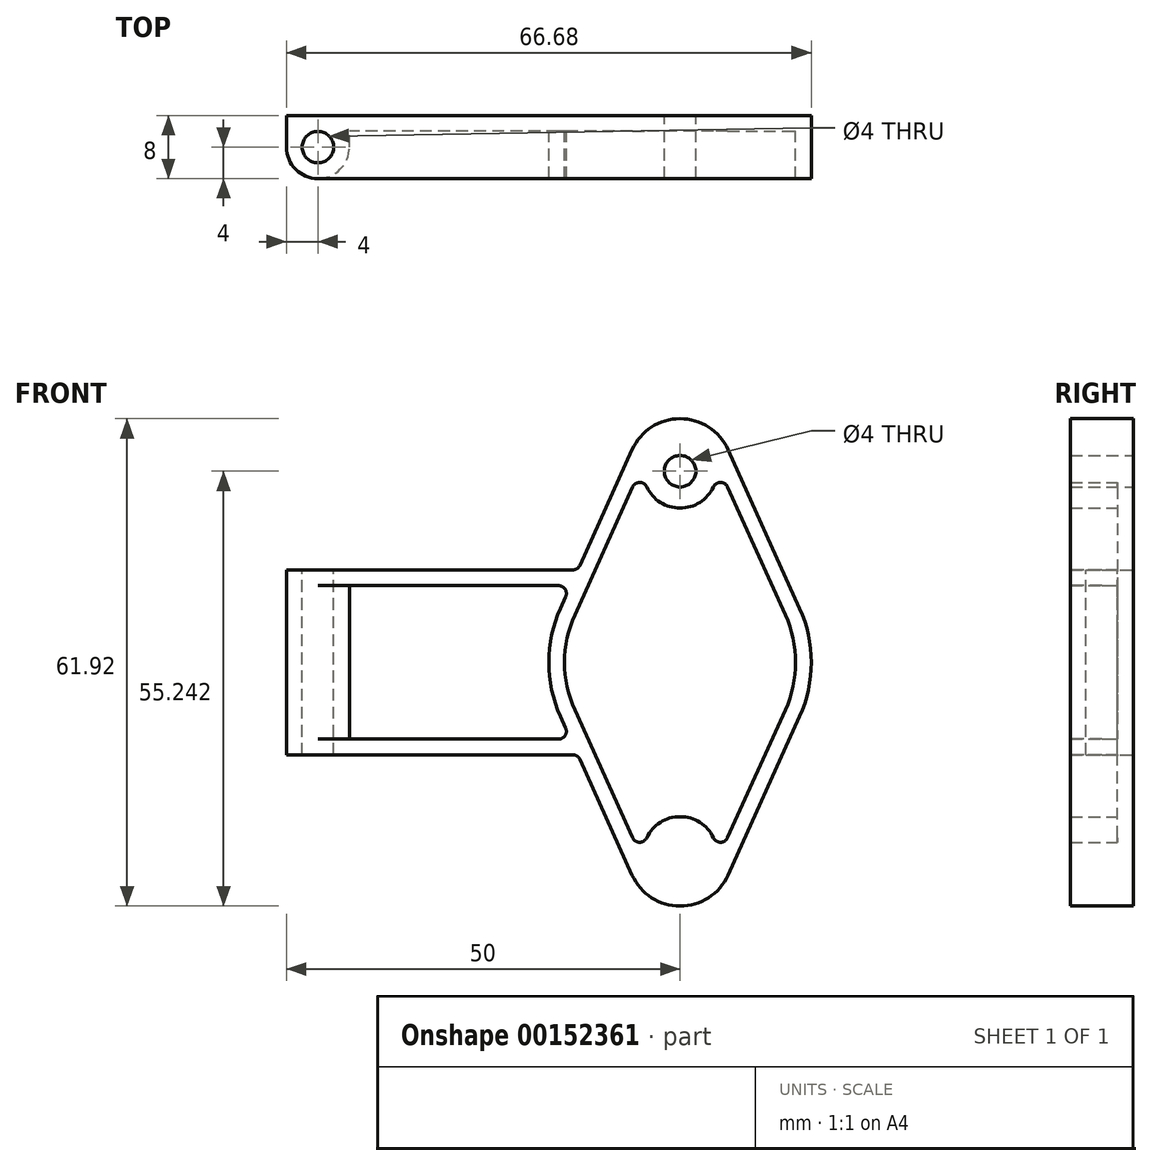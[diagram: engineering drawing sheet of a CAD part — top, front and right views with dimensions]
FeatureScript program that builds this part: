
annotation { "Feature Type Name" : "Feature", "Feature Type Description" : "" }
export const myFeature = defineFeature(function(context is Context, id is Id, definition is map)
    precondition{}
    {
        {
            var Q0;
            Q0=qCreatedBy(makeId("Front.planeOp"),FACE);
            var sketch = newSketch(context, id + "F0", { "sketchPlane" : qUnion([Q0])});
            skArc(sketch, "E0", {"start": v(6.09, 27.03) * mm, "mid": v(0, 30.96) * mm, "end": v(-6.09, 27.03) * mm});
            skArc(sketch, "E1.MirrorC", {"start": v(6.09, -27.03) * mm, "mid": v(0, -30.96) * mm, "end": v(-6.09, -27.03) * mm});
            skArc(sketch, "E2", {"start": v(-15.2, 6.86) * mm, "mid": v(-16.68, 0) * mm, "end": v(-15.2, -6.86) * mm});
            skLineSegment(sketch, "E3", {"start": v(-6.09, 27.03) * mm, "end": v(-15.2, 6.86) * mm});
            skLineSegment(sketch, "E4.MirrorCS", {"start": v(-6.09, -27.03) * mm, "end": v(-15.2, -6.86) * mm});
            skLineSegment(sketch, "E5.MirrorCS", {"start": v(6.09, 27.03) * mm, "end": v(15.2, 6.86) * mm});
            skLineSegment(sketch, "E6.MirrorCS", {"start": v(6.09, -27.03) * mm, "end": v(15.2, -6.86) * mm});
            skArc(sketch, "E7.trimOffspring", {"start": v(15.2, -6.86) * mm, "mid": v(16.68, 0) * mm, "end": v(15.2, 6.86) * mm});
            skCircle(sketch, "E8", {"center": v(0, 24.28) * mm, "radius": 2 * mm});
            skCircle(sketch, "E9.MirrorC", {"center": v(0, -24.28) * mm, "radius": 2 * mm});
            skLineSegment(sketch, "E10.1", {"start": v(-6.05, 22.27) * mm, "end": v(-13.37, 6.04) * mm});
            skLineSegment(sketch, "E10.2", {"start": v(6.05, 22.27) * mm, "end": v(13.37, 6.04) * mm});
            skArc(sketch, "E10.3", {"start": v(-13.37, 6.04) * mm, "mid": v(-14.68, 0) * mm, "end": v(-13.37, -6.04) * mm});
            skArc(sketch, "E10.4", {"start": v(13.37, -6.04) * mm, "mid": v(14.68, 0) * mm, "end": v(13.37, 6.04) * mm});
            skLineSegment(sketch, "E10.5", {"start": v(6.05, -22.27) * mm, "end": v(13.37, -6.04) * mm});
            skLineSegment(sketch, "E10.7", {"start": v(-6.05, -22.27) * mm, "end": v(-13.37, -6.04) * mm});
            skArc(sketch, "E11", {"start": v(-4.23, 22.28) * mm, "mid": v(0, 19.6) * mm, "end": v(4.23, 22.28) * mm});
            skArc(sketch, "E12", {"start": v(4.23, -22.28) * mm, "mid": v(0, -19.6) * mm, "end": v(-4.23, -22.28) * mm});
            skPoint(sketch, "E13.visualSharp", {"position": v(-4.27, 26.2) * mm});
            skArc(sketch, "E13.filletArc", {"start": v(-4.23, 22.28) * mm, "mid": v(-5.14, 22.85) * mm, "end": v(-6.05, 22.27) * mm});
            skPoint(sketch, "E14.visualSharp", {"position": v(4.27, 26.2) * mm});
            skArc(sketch, "E14.filletArc", {"start": v(6.05, 22.27) * mm, "mid": v(5.14, 22.85) * mm, "end": v(4.23, 22.28) * mm});
            skPoint(sketch, "E15.visualSharp", {"position": v(4.27, -26.2) * mm});
            skArc(sketch, "E15.filletArc", {"start": v(4.23, -22.28) * mm, "mid": v(5.14, -22.85) * mm, "end": v(6.05, -22.27) * mm});
            skPoint(sketch, "E16.visualSharp", {"position": v(-4.27, -26.2) * mm});
            skArc(sketch, "E16.filletArc", {"start": v(-6.05, -22.27) * mm, "mid": v(-5.14, -22.85) * mm, "end": v(-4.23, -22.28) * mm});
            skLineSegment(sketch, "E17", {"start": v(-50, 11.75) * mm, "end": v(-13, 11.75) * mm});
            skLineSegment(sketch, "E18.MirrorCS", {"start": v(-50, -11.75) * mm, "end": v(-13, -11.75) * mm});
            skLineSegment(sketch, "E19", {"start": v(-50, 11.75) * mm, "end": v(-50, -11.75) * mm});
            skLineSegment(sketch, "E20", {"start": v(-13.9, 9.75) * mm, "end": v(-42, 9.75) * mm});
            skLineSegment(sketch, "E21", {"start": v(-42, 9.75) * mm, "end": v(-42, -9.75) * mm});
            skLineSegment(sketch, "E22.MirrorCS", {"start": v(-13.9, -9.75) * mm, "end": v(-42, -9.75) * mm});
            skSolve(sketch);
        }
        {
            var Q0;
            Q0=makeQuery(id+"F0.imprint","IMPRINT",FACE,{"disambiguationData":[TD([[makeQuery(id+"F0.imprint","IMPRINT",EDGE,{"derivedFrom":sQuery(id+"F0.wireOp",EDGE,"E0")}),1.0]])]});
            var Q1;
            Q1=makeQuery(id+"F0.imprint","IMPRINT",FACE,{"disambiguationData":[TD([[makeQuery(id+"F0.imprint","IMPRINT",EDGE,{"derivedFrom":sQuery(id+"F0.wireOp",EDGE,"3e905b6d-8bee-4998-9225-6dcc00ec54d6.0")}),1.0]])]});
            var Q2;
            {var subQ0=sQuery(id+"F0.wireOp",EDGE,"V3VQVJa9-jFdV-kq6X-8dhK-Xa6uhI9IwXRv");Q2=makeQuery(id+"F0.imprint","IMPRINT",FACE,{"disambiguationData":[TD([[makeQuery(id+"F0.imprint","IMPRINT",EDGE,{"derivedFrom":subQ0}),1.0]])]});}
            var Q3;
            {var subQ0=sQuery(id+"F0.wireOp",EDGE,"fO4OrWz9-9ff7-9GLH-ZSri-iVDJwJIuYxIB");Q3=makeQuery(id+"F0.imprint","IMPRINT",FACE,{"disambiguationData":[TD([[makeQuery(id+"F0.imprint","IMPRINT",EDGE,{"derivedFrom":subQ0}),1.0]])]});}
            var Q4;
            Q4=makeQuery(id+"F0.imprint","IMPRINT",FACE,{"disambiguationData":[TD([[makeQuery(id+"F0.imprint","IMPRINT",EDGE,{"derivedFrom":sQuery(id+"F0.wireOp",EDGE,"E9.MirrorC")}),1.0]])]});
            var Q5;
            Q5=makeQuery(id+"F0.imprint","IMPRINT",FACE,{"disambiguationData":[TD([[makeQuery(id+"F0.imprint","IMPRINT",EDGE,{"derivedFrom":sQuery(id+"F0.wireOp",EDGE,"E8")}),-1.0]])]});
            var Q6;
            {var subQ1=sQuery(id+"F0.wireOp",EDGE,"E17");Q6=makeQuery(id+"F0.imprint","IMPRINT",FACE,{"disambiguationData":[TD([[makeQuery(id+"F0.imprint","IMPRINT",EDGE,{"derivedFrom":subQ1}),-1.0]])]});}
            extrude(context, id + "F1", {"entities" : qUnion([Q0, Q1, Q2, Q3, Q4, Q5, Q6]), "depth" : 8 * mm});
        }
        {
            var Q0;
            {var subQ2=sQuery(id+"F0.wireOp",EDGE,"E10.1");Q0=makeQuery(id+"F0.imprint","IMPRINT",FACE,{"disambiguationData":[TD([[makeQuery(id+"F0.imprint","IMPRINT",EDGE,{"derivedFrom":subQ2}),1.0]])]});}
            var Q1;
            {var subQ1=sQuery(id+"F0.wireOp",EDGE,"E1.MirrorC");Q1=makeQuery(id+"F0.imprint","IMPRINT",FACE,{"disambiguationData":[TD([[makeQuery(id+"F0.imprint","IMPRINT",EDGE,{"derivedFrom":subQ1}),1.0]])]});}
            var Q2;
            {var subQ1=sQuery(id+"F0.wireOp",EDGE,"E2");Q2=makeQuery(id+"F0.imprint","IMPRINT",FACE,{"disambiguationData":[TD([[makeQuery(id+"F0.imprint","IMPRINT",EDGE,{"derivedFrom":subQ1}),-1.0]])]});}
            extrude(context, id + "F2", {"entities" : qUnion([Q0, Q1, Q2]), "operationType" : NewBodyOperationType.ADD, "depth" : 2 * mm});
        }
        {
            var Q0;
            Q0=makeQuery(id+"F1.opExtrude","SWEPT_EDGE",EDGE,{"disambiguationData":[OSD([sQuery(id+"F0.wireOp",EDGE,"E4.MirrorCS"),sQuery(id+"F0.wireOp",EDGE,"E22.MirrorCS")])]});
            var Q1;
            Q1=makeQuery(id+"F1.opExtrude","SWEPT_EDGE",EDGE,{"disambiguationData":[OSD([sQuery(id+"F0.wireOp",EDGE,"E4.MirrorCS"),sQuery(id+"F0.wireOp",EDGE,"E18.MirrorCS")])]});
            var Q2;
            Q2=makeQuery(id+"F1.opExtrude","SWEPT_EDGE",EDGE,{"disambiguationData":[OSD([sQuery(id+"F0.wireOp",EDGE,"E3"),sQuery(id+"F0.wireOp",EDGE,"E20")])]});
            var Q3;
            Q3=makeQuery(id+"F1.opExtrude","SWEPT_EDGE",EDGE,{"disambiguationData":[OSD([sQuery(id+"F0.wireOp",EDGE,"E3"),sQuery(id+"F0.wireOp",EDGE,"E17")])]});
            fillet(context, id + "F3", {"entities" : qUnion([Q0, Q1, Q2, Q3]), "radius" : 1 * mm, "tangentPropagation" : true, "allowEdgeOverflow" : false});
        }
        {
            var Q0;
            Q0=makeQuery(id+"F1.opExtrude","SWEPT_FACE",FACE,{"disambiguationData":[OSD([sQuery(id+"F0.wireOp",EDGE,"E17")])]});
            var sketch = newSketch(context, id + "F4", { "sketchPlane" : qUnion([Q0])});
            skPoint(sketch, "E23", {"position": v(-46, -4) * mm});
            skLineSegment(sketch, "E24", {"start": v(-50, 0) * mm, "end": v(-46, -4) * mm, "construction": true});
            skLineSegment(sketch, "E25", {"start": v(-46, -4) * mm, "end": v(-50, -8) * mm, "construction": true});
            skSolve(sketch);
        }
        {
            var Q0;
            Q0=sQuery(id+"F4.wireOp",VERTEX,"E23");
            var Q1;
            Q1=makeQuery(id+"F1.opExtrude","SWEPT_BODY",BODY,{"disambiguationData":[OSD([sQuery(id+"F0.wireOp",EDGE,"E0"),sQuery(id+"F0.wireOp",EDGE,"E2"),sQuery(id+"F0.wireOp",EDGE,"E3"),sQuery(id+"F0.wireOp",EDGE,"E5.MirrorCS"),sQuery(id+"F0.wireOp",EDGE,"E7.trimOffspring"),sQuery(id+"F0.wireOp",EDGE,"S2IiUO7s-7rjS-UU1n-G3Er-isHJvikYOna3"),sQuery(id+"F0.wireOp",EDGE,"U4xu2M48-wPnJ-tMoa-V4Px-PJSouQ81H8F5"),sQuery(id+"F0.wireOp",EDGE,"HV652KFt-d8Xn-WSbo-tHCJ-cfUj0g3Xd7DK"),sQuery(id+"F0.wireOp",EDGE,"fO4OrWz9-9ff7-9GLH-ZSri-iVDJwJIuYxIB"),sQuery(id+"F0.wireOp",EDGE,"zmEnNPUg-k7De-l4Ih-Irfg-M27UcczaaJBl"),sQuery(id+"F0.wireOp",EDGE,"V3VQVJa9-jFdV-kq6X-8dhK-Xa6uhI9IwXRv"),sQuery(id+"F0.wireOp",EDGE,"W1IEodJy-6PRz-xiH1-2iNf-kAuRcIV7mYlj"),sQuery(id+"F0.wireOp",EDGE,"5ZKJKvnk-ET5z-qlB3-oLW5-LuLVHKlnV0HX"),sQuery(id+"F0.wireOp",EDGE,"Gk8awqwg-zgXA-VnUW-8MKI-QdblR6Wf13JX"),sQuery(id+"F0.wireOp",EDGE,"WIDdAYBM-okhh-eBsl-QBhJ-HuDdJqstO0Cl"),sQuery(id+"F0.wireOp",EDGE,"iXw4nrh7-EQqi-IiG2-VBaK-kNldmVsmUaTg"),sQuery(id+"F0.wireOp",EDGE,"03ff63bc-461f-42e4-a166-82e271801758"),sQuery(id+"F0.wireOp",EDGE,"5881da14-4dba-48e3-8e12-341ecdeeb7140.MirrorCS")])]});
            hole(context, id + "F5", {"style" : HoleStyle.SIMPLE, "endStyle" : HoleEndStyle.THROUGH, "standardTappedOrClearance" : lookupTablePath({ "standard" : "ISO", "size" : "4", "type" : "Drilled" }), "standardBlindInLast" : lookupTablePath({ "standard" : "ISO", "size" : "4", "type" : "Drilled" }), "holeDiameter" : 4 * mm, "locations" : qUnion([Q0]), "scope" : qUnion([Q1]), "isTappedThrough" : true});
        }
        {
            var Q0;
            Q0=makeQuery(id+"F1.opExtrude","CAP_EDGE",EDGE,{"disambiguationData":[OSD([sQuery(id+"F0.wireOp",EDGE,"E19")])],"isStart":false});
            var Q1;
            Q1=makeQuery(id+"F1.opExtrude","CAP_EDGE",EDGE,{"disambiguationData":[OSD([sQuery(id+"F0.wireOp",EDGE,"E21")])],"isStart":false});
            fillet(context, id + "F6", {"entities" : qUnion([Q0, Q1]), "radius" : (8 / 2) * mm, "tangentPropagation" : true, "allowEdgeOverflow" : false});
        }
    });
